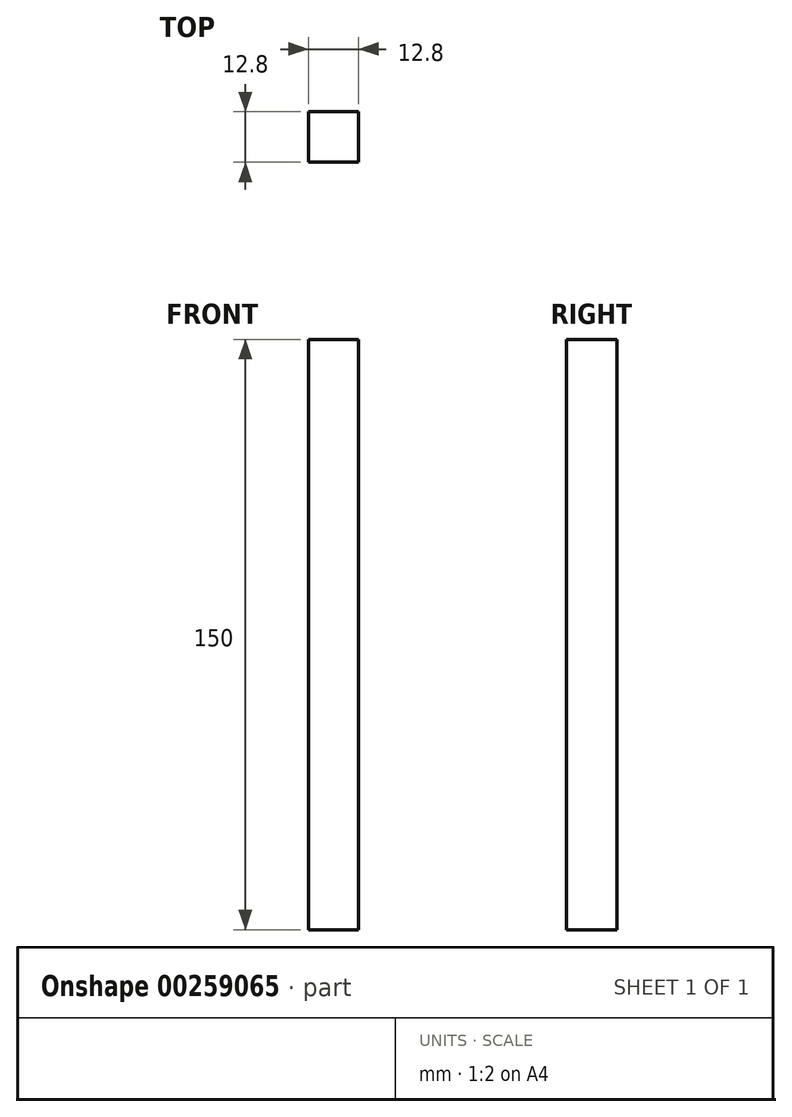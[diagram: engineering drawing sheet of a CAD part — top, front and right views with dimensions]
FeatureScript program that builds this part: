
annotation { "Feature Type Name" : "Feature", "Feature Type Description" : "" }
export const myFeature = defineFeature(function(context is Context, id is Id, definition is map)
    precondition{}
    {
        {
            var Q0;
            Q0=qCreatedBy(makeId("Top.planeOp"),FACE);
            var sketch = newSketch(context, id + "F0", { "sketchPlane" : qUnion([Q0])});
            skLineSegment(sketch, "E0.bottom", {"start": v(6.4, -6.4) * mm, "end": v(-6.4, -6.4) * mm});
            skLineSegment(sketch, "E0.top", {"start": v(6.4, 6.4) * mm, "end": v(-6.4, 6.4) * mm});
            skLineSegment(sketch, "E0.left", {"start": v(6.4, -6.4) * mm, "end": v(6.4, 6.4) * mm});
            skLineSegment(sketch, "E0.right", {"start": v(-6.4, -6.4) * mm, "end": v(-6.4, 6.4) * mm});
            skPoint(sketch, "E0.middle", {"position": v(0, 0) * mm});
            skSolve(sketch);
        }
        {
            var Q0;
            Q0 = qSketchRegion(id + "F0", true);
            extrude(context, id + "F1", {"entities" : qUnion([Q0]), "depth" : 150 * mm});
        }
    });
